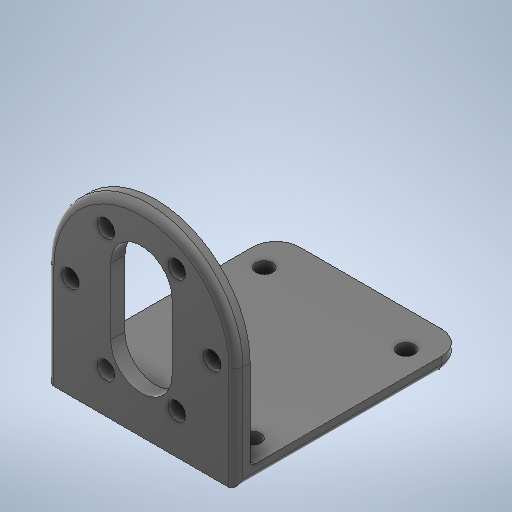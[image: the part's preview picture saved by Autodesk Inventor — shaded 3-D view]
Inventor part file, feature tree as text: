
AUTODESK INVENTOR PART (.ipt)
format: ipt  version: 2025.2 (Build 292293000, 293)  size: 416,768 bytes
history: native  units: mm
features: sketch x11, extrude x7, fillet x4, projected_geometry x4
ambient origin geometry x8: Origin, YZ Plane, XZ Plane, XY Plane, X Axis, Y Axis, Z Axis, Center Point
bodies: Solid1 (feature_tree)
feature tree (26):
  extrude  "Extrusion1"  Depth=47.5mm
  extrude  "Extrusion2"  Depth=40.0mm
  fillet  "Fillet1"  Radius=40.0mm
  extrude  "Extrusion3"  Depth=13.0mm
  fillet  "Fillet2"  Radius=3.0mm
  extrude  "Extrusion4"  Depth=40.0mm TaperAngle=0.0deg
  extrude  "Extrusion5"  Depth=3.5mm
  extrude  "Extrusion8"  TaperAngle=90.0deg  [1 undecoded]
  extrude  "Extrusion9"  TaperAngle=90.0deg  [1 undecoded]
  fillet  "Fillet4"  Radius=40.0mm
  fillet  "Fillet5"  Radius=5.0mm
  sketch  "Sketch1"  dims[d0=2.0mm d1=47.5mm]
  sketch  "Sketch2"  dims[d9=60.0mm d11=360.0deg d13=40.0mm d14=0.0mm]
  sketch  "Sketch Circular Pattern1"  dims[d2=41.0mm d3=2.0mm d4=40.0mm d5=0.0mm]
  sketch  "Sketch3"  dims[d17=32.5mm d18=90.0deg]
  sketch  "Sketch Rectangular Pattern1"  dims[d6=14.0mm d7=13.0mm d8=3.0mm]
  sketch  "Sketch4"  dims[d21=20.0mm d23=32.5mm d24=20.0mm d26=30.0mm d29=40.0mm d30=0.0mm d31=5.0mm]
  projected_geometry  "Projected Loop1"
  sketch  "Sketch5"  dims[d37=10.0mm d38=0.0mm]
  projected_geometry  "Projected Loop2"
  sketch  "Sketch Rectangular Pattern2"  dims[d15=20.0mm d16=3.5mm]
  sketch  "Sketch Circular Pattern3"  dims[d19=30.0mm d20=90.0deg]
  sketch  "Sketch8"  dims[d47=0.05mm]
  projected_geometry  "Projected Loop5"
  sketch  "Sketch9"  dims[d48=20.0mm d50=32.5mm d51=20.0mm d53=30.0mm d56=10.0mm d57=0.0mm d58=3.75mm d59=60.0mm d61=360.0deg d68=1.0mm d69=0.0mm d70=1.0mm d71=0.0mm d72=1.5mm d73=1.0mm]
  projected_geometry  "Projected Loop6"
note: 2 required parameter values undecoded (feature->parameter linkage not recoverable at this tier; creation-order binding heuristic only, values carry confidence <= 0.55)
